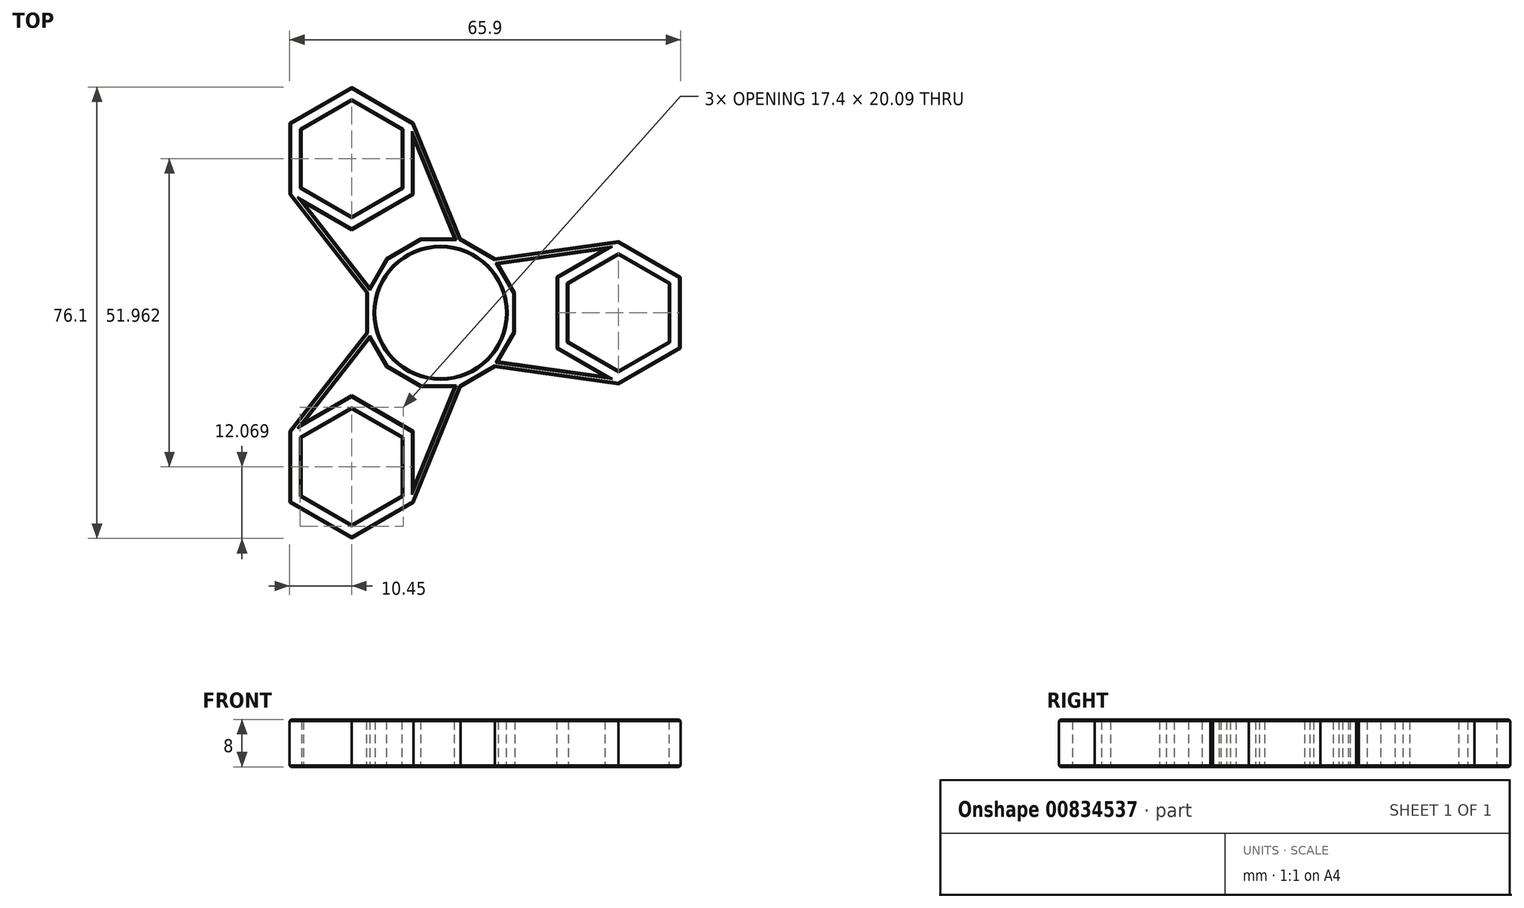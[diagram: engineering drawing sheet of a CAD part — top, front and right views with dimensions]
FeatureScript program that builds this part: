
annotation { "Feature Type Name" : "Feature", "Feature Type Description" : "" }
export const myFeature = defineFeature(function(context is Context, id is Id, definition is map)
    precondition{}
    {
        {
            var Q0;
            Q0=qCreatedBy(makeId("Top.planeOp"),FACE);
            var sketch = newSketch(context, id + "F0", { "sketchPlane" : qUnion([Q0])});
            skCircle(sketch, "E0", {"center": v(0, 0) * mm, "radius": 11.05 * mm});
            skCircle(sketch, "E1.cCircle", {"center": v(30, 0) * mm, "radius": 8.45 * mm, "construction": true});
            skLineSegment(sketch, "E1.0", {"start": v(30, 9.76) * mm, "end": v(38.45, 4.88) * mm});
            skLineSegment(sketch, "E1.1", {"start": v(38.45, 4.88) * mm, "end": v(38.45, -4.88) * mm});
            skLineSegment(sketch, "E1.2", {"start": v(38.45, -4.88) * mm, "end": v(30, -9.76) * mm});
            skLineSegment(sketch, "E1.3", {"start": v(30, -9.76) * mm, "end": v(21.55, -4.88) * mm});
            skLineSegment(sketch, "E1.4", {"start": v(21.55, -4.88) * mm, "end": v(21.55, 4.88) * mm});
            skLineSegment(sketch, "E1.5", {"start": v(21.55, 4.88) * mm, "end": v(30, 9.76) * mm});
            skPoint(sketch, "E1.0.midPoint", {"position": v(34.23, 7.32) * mm});
            skLineSegment(sketch, "E2.1.0", {"start": v(-15, 16.22) * mm, "end": v(-23.45, 21.1) * mm});
            skLineSegment(sketch, "E2.1.1", {"start": v(-6.55, 21.1) * mm, "end": v(-15, 16.22) * mm});
            skLineSegment(sketch, "E2.1.2", {"start": v(-23.45, 21.1) * mm, "end": v(-23.45, 30.86) * mm});
            skLineSegment(sketch, "E2.1.3", {"start": v(-23.45, 30.86) * mm, "end": v(-15, 35.74) * mm});
            skLineSegment(sketch, "E2.1.4", {"start": v(-15, 35.74) * mm, "end": v(-6.55, 30.86) * mm});
            skLineSegment(sketch, "E2.1.5", {"start": v(-6.55, 30.86) * mm, "end": v(-6.55, 21.1) * mm});
            skLineSegment(sketch, "E2.2.0", {"start": v(-6.55, -21.1) * mm, "end": v(-6.55, -30.86) * mm});
            skLineSegment(sketch, "E2.2.1", {"start": v(-15, -16.22) * mm, "end": v(-6.55, -21.1) * mm});
            skLineSegment(sketch, "E2.2.2", {"start": v(-6.55, -30.86) * mm, "end": v(-15, -35.74) * mm});
            skLineSegment(sketch, "E2.2.3", {"start": v(-15, -35.74) * mm, "end": v(-23.45, -30.86) * mm});
            skLineSegment(sketch, "E2.2.4", {"start": v(-23.45, -30.86) * mm, "end": v(-23.45, -21.1) * mm});
            skLineSegment(sketch, "E2.2.5", {"start": v(-23.45, -21.1) * mm, "end": v(-15, -16.22) * mm});
            skSolve(sketch);
        }
        {
            var Q0;
            Q0=qCreatedBy(makeId("Top.planeOp"),FACE);
            var sketch = newSketch(context, id + "F1", { "sketchPlane" : qUnion([Q0])});
            skLineSegment(sketch, "E3.0.0", {"start": v(-6.55, 21.1) * mm, "end": v(-6.55, 30.86) * mm});
            skLineSegment(sketch, "E3.0.1", {"start": v(-6.55, 30.86) * mm, "end": v(-15, 35.74) * mm});
            skLineSegment(sketch, "E3.0.2", {"start": v(-15, 35.74) * mm, "end": v(-23.45, 30.86) * mm});
            skLineSegment(sketch, "E3.0.3", {"start": v(-23.45, 30.86) * mm, "end": v(-23.45, 21.1) * mm});
            skLineSegment(sketch, "E3.0.4", {"start": v(-23.45, 21.1) * mm, "end": v(-15, 16.22) * mm});
            skLineSegment(sketch, "E3.0.5", {"start": v(-15, 16.22) * mm, "end": v(-6.55, 21.1) * mm});
            skLineSegment(sketch, "E4.0.0", {"start": v(-15, -16.22) * mm, "end": v(-23.45, -21.1) * mm});
            skLineSegment(sketch, "E4.0.1", {"start": v(-23.45, -21.1) * mm, "end": v(-23.45, -30.86) * mm});
            skLineSegment(sketch, "E4.0.2", {"start": v(-23.45, -30.86) * mm, "end": v(-15, -35.74) * mm});
            skLineSegment(sketch, "E4.0.3", {"start": v(-15, -35.74) * mm, "end": v(-6.55, -30.86) * mm});
            skLineSegment(sketch, "E4.0.4", {"start": v(-6.55, -30.86) * mm, "end": v(-6.55, -21.1) * mm});
            skLineSegment(sketch, "E4.0.5", {"start": v(-6.55, -21.1) * mm, "end": v(-15, -16.22) * mm});
            skLineSegment(sketch, "E5.0.0", {"start": v(30, 9.76) * mm, "end": v(21.55, 4.88) * mm});
            skLineSegment(sketch, "E5.0.1", {"start": v(21.55, 4.88) * mm, "end": v(21.55, -4.88) * mm});
            skLineSegment(sketch, "E5.0.2", {"start": v(21.55, -4.88) * mm, "end": v(30, -9.76) * mm});
            skLineSegment(sketch, "E5.0.3", {"start": v(30, -9.76) * mm, "end": v(38.45, -4.88) * mm});
            skLineSegment(sketch, "E5.0.4", {"start": v(38.45, -4.88) * mm, "end": v(38.45, 4.88) * mm});
            skLineSegment(sketch, "E5.0.5", {"start": v(38.45, 4.88) * mm, "end": v(30, 9.76) * mm});
            skCircle(sketch, "E6.0.0", {"center": v(0, 0) * mm, "radius": 11.05 * mm});
            skLineSegment(sketch, "E7", {"start": v(-23.45, 30.86) * mm, "end": v(-6.55, 21.1) * mm, "construction": true});
            skLineSegment(sketch, "E8", {"start": v(-23.45, -30.86) * mm, "end": v(-6.55, -21.1) * mm, "construction": true});
            skLineSegment(sketch, "E9", {"start": v(21.55, 4.88) * mm, "end": v(38.45, -4.88) * mm, "construction": true});
            skLineSegment(sketch, "E10.0", {"start": v(40.45, -6.03) * mm, "end": v(40.45, 6.03) * mm});
            skLineSegment(sketch, "E10.1", {"start": v(30, 12.07) * mm, "end": v(19.55, 6.03) * mm});
            skLineSegment(sketch, "E10.2", {"start": v(19.55, 6.03) * mm, "end": v(19.55, -6.03) * mm});
            skLineSegment(sketch, "E10.3", {"start": v(40.45, 6.03) * mm, "end": v(30, 12.07) * mm});
            skLineSegment(sketch, "E10.4", {"start": v(19.55, -6.03) * mm, "end": v(30, -12.07) * mm});
            skLineSegment(sketch, "E10.5", {"start": v(30, -12.07) * mm, "end": v(40.45, -6.03) * mm});
            skCircle(sketch, "E11.cCircle", {"center": v(0, 0) * mm, "radius": 12.5 * mm, "construction": true});
            skLineSegment(sketch, "E11.0", {"start": v(3.35, 12.5) * mm, "end": v(9.15, 9.15) * mm});
            skLineSegment(sketch, "E11.1", {"start": v(9.15, 9.15) * mm, "end": v(12.5, 3.35) * mm});
            skLineSegment(sketch, "E11.2", {"start": v(12.5, 3.35) * mm, "end": v(12.5, -3.35) * mm});
            skLineSegment(sketch, "E11.3", {"start": v(12.5, -3.35) * mm, "end": v(9.15, -9.15) * mm});
            skLineSegment(sketch, "E11.4", {"start": v(9.15, -9.15) * mm, "end": v(3.35, -12.5) * mm});
            skLineSegment(sketch, "E11.5", {"start": v(3.35, -12.5) * mm, "end": v(-3.35, -12.5) * mm});
            skLineSegment(sketch, "E11.6", {"start": v(-3.35, -12.5) * mm, "end": v(-9.15, -9.15) * mm});
            skLineSegment(sketch, "E11.7", {"start": v(-9.15, -9.15) * mm, "end": v(-12.5, -3.35) * mm});
            skLineSegment(sketch, "E11.8", {"start": v(-12.5, -3.35) * mm, "end": v(-12.5, 3.35) * mm});
            skLineSegment(sketch, "E11.9", {"start": v(-12.5, 3.35) * mm, "end": v(-9.15, 9.15) * mm});
            skLineSegment(sketch, "E11.10", {"start": v(-9.15, 9.15) * mm, "end": v(-3.35, 12.5) * mm});
            skLineSegment(sketch, "E11.11", {"start": v(-3.35, 12.5) * mm, "end": v(3.35, 12.5) * mm});
            skPoint(sketch, "E11.0.midPoint", {"position": v(6.25, 10.83) * mm});
            skLineSegment(sketch, "E12", {"start": v(30, 12.07) * mm, "end": v(9.15, 9.15) * mm});
            skLineSegment(sketch, "E13", {"start": v(30, -12.07) * mm, "end": v(9.15, -9.15) * mm});
            skLineSegment(sketch, "E14.0", {"start": v(30.14, 11.08) * mm, "end": v(9.29, 8.16) * mm});
            skLineSegment(sketch, "E15.0", {"start": v(30.14, -11.08) * mm, "end": v(9.29, -8.16) * mm});
            skLineSegment(sketch, "E16.0", {"start": v(-25.45, -19.95) * mm, "end": v(-25.45, -32.01) * mm});
            skLineSegment(sketch, "E16.1", {"start": v(-15, -38.05) * mm, "end": v(-4.55, -32.01) * mm});
            skLineSegment(sketch, "E16.2", {"start": v(-4.55, -32.01) * mm, "end": v(-4.55, -19.95) * mm});
            skLineSegment(sketch, "E16.3", {"start": v(-25.45, -32.01) * mm, "end": v(-15, -38.05) * mm});
            skLineSegment(sketch, "E16.4", {"start": v(-4.55, -19.95) * mm, "end": v(-15, -13.91) * mm});
            skLineSegment(sketch, "E16.5", {"start": v(-15, -13.91) * mm, "end": v(-25.45, -19.95) * mm});
            skLineSegment(sketch, "E17.0", {"start": v(-4.55, 19.95) * mm, "end": v(-4.55, 32.01) * mm});
            skLineSegment(sketch, "E17.1", {"start": v(-15, 38.05) * mm, "end": v(-25.45, 32.01) * mm});
            skLineSegment(sketch, "E17.2", {"start": v(-25.45, 32.01) * mm, "end": v(-25.45, 19.95) * mm});
            skLineSegment(sketch, "E17.3", {"start": v(-4.55, 32.01) * mm, "end": v(-15, 38.05) * mm});
            skLineSegment(sketch, "E17.4", {"start": v(-25.45, 19.95) * mm, "end": v(-15, 13.91) * mm});
            skLineSegment(sketch, "E17.5", {"start": v(-15, 13.91) * mm, "end": v(-4.55, 19.95) * mm});
            skLineSegment(sketch, "E18", {"start": v(-25.45, 19.95) * mm, "end": v(-12.5, 3.35) * mm});
            skLineSegment(sketch, "E19", {"start": v(-4.55, 32.01) * mm, "end": v(3.35, 12.5) * mm});
            skLineSegment(sketch, "E20", {"start": v(-25.45, -19.95) * mm, "end": v(-12.5, -3.35) * mm});
            skLineSegment(sketch, "E21", {"start": v(3.35, -12.5) * mm, "end": v(-4.55, -32.01) * mm});
            skLineSegment(sketch, "E22.0", {"start": v(-24.66, 20.56) * mm, "end": v(-11.71, 3.96) * mm});
            skLineSegment(sketch, "E23.0", {"start": v(-5.48, 31.64) * mm, "end": v(2.42, 12.12) * mm});
            skLineSegment(sketch, "E24.0", {"start": v(-24.66, -20.56) * mm, "end": v(-11.71, -3.96) * mm});
            skLineSegment(sketch, "E25.0", {"start": v(2.42, -12.12) * mm, "end": v(-5.48, -31.64) * mm});
            skSolve(sketch);
        }
        {
            var Q0;
            Q0=makeQuery(id+"F1.imprint","IMPRINT",FACE,{"disambiguationData":[TD([[makeQuery(id+"F1.imprint","IMPRINT",EDGE,{"derivedFrom":sQuery(id+"F1.wireOp",EDGE,"E6.0.0")}),-1.0]])]});
            var Q1;
            Q1=makeQuery(id+"F1.imprint","IMPRINT",FACE,{"disambiguationData":[TD([[makeQuery(id+"F1.imprint","IMPRINT",EDGE,{"derivedFrom":sQuery(id+"F1.wireOp",EDGE,"E5.0.0")}),-1.0]])]});
            var Q2;
            {var subQ0=sQuery(id+"F1.wireOp",EDGE,"E13");Q2=makeQuery(id+"F1.imprint","IMPRINT",FACE,{"disambiguationData":[TD([[makeQuery(id+"F1.imprint","IMPRINT",EDGE,{"derivedFrom":subQ0}),-1.0]])]});}
            var Q3;
            {var subQ0=sQuery(id+"F1.wireOp",EDGE,"E12");Q3=makeQuery(id+"F1.imprint","IMPRINT",FACE,{"disambiguationData":[TD([[makeQuery(id+"F1.imprint","IMPRINT",EDGE,{"derivedFrom":subQ0}),1.0]])]});}
            var Q4;
            Q4=makeQuery(id+"F1.imprint","IMPRINT",FACE,{"disambiguationData":[TD([[makeQuery(id+"F1.imprint","IMPRINT",EDGE,{"derivedFrom":sQuery(id+"F1.wireOp",EDGE,"E4.0.0")}),-1.0]])]});
            var Q5;
            Q5=makeQuery(id+"F1.imprint","IMPRINT",FACE,{"disambiguationData":[TD([[makeQuery(id+"F1.imprint","IMPRINT",EDGE,{"derivedFrom":sQuery(id+"F1.wireOp",EDGE,"E3.0.0")}),-1.0]])]});
            var Q6;
            Q6=makeQuery(id+"F1.imprint","IMPRINT",FACE,{"disambiguationData":[TD([[makeQuery(id+"F1.imprint","IMPRINT",EDGE,{"derivedFrom":sQuery(id+"F1.wireOp",EDGE,"E11.9")}),1.0]])]});
            var Q7;
            Q7=makeQuery(id+"F1.imprint","IMPRINT",FACE,{"disambiguationData":[TD([[makeQuery(id+"F1.imprint","IMPRINT",EDGE,{"derivedFrom":sQuery(id+"F1.wireOp",EDGE,"E11.11")}),1.0]])]});
            var Q8;
            {var subQ0=sQuery(id+"F1.wireOp",EDGE,"E20");Q8=makeQuery(id+"F1.imprint","IMPRINT",FACE,{"disambiguationData":[TD([[makeQuery(id+"F1.imprint","IMPRINT",EDGE,{"derivedFrom":subQ0}),-1.0]])]});}
            var Q9;
            {var subQ0=sQuery(id+"F1.wireOp",EDGE,"E21");Q9=makeQuery(id+"F1.imprint","IMPRINT",FACE,{"disambiguationData":[TD([[makeQuery(id+"F1.imprint","IMPRINT",EDGE,{"derivedFrom":subQ0}),-1.0]])]});}
            extrude(context, id + "F2", {"entities" : qUnion([Q0, Q1, Q2, Q3, Q4, Q5, Q6, Q7, Q8, Q9]), "depth" : 8 * mm, "offsetDistance" : 25 * mm});
        }
        {
            var Q0;
            Q0=makeQuery(id+"F2.opExtrude","CAP_FACE",FACE,{"disambiguationData":[OSD([sQuery(id+"F1.wireOp",EDGE,"E3.0.0"),sQuery(id+"F1.wireOp",EDGE,"E3.0.1"),sQuery(id+"F1.wireOp",EDGE,"E3.0.2"),sQuery(id+"F1.wireOp",EDGE,"E3.0.3"),sQuery(id+"F1.wireOp",EDGE,"E3.0.4"),sQuery(id+"F1.wireOp",EDGE,"E3.0.5"),sQuery(id+"F1.wireOp",EDGE,"E4.0.0"),sQuery(id+"F1.wireOp",EDGE,"E4.0.1"),sQuery(id+"F1.wireOp",EDGE,"E4.0.2"),sQuery(id+"F1.wireOp",EDGE,"E4.0.3"),sQuery(id+"F1.wireOp",EDGE,"E4.0.4"),sQuery(id+"F1.wireOp",EDGE,"E4.0.5"),sQuery(id+"F1.wireOp",EDGE,"E5.0.0"),sQuery(id+"F1.wireOp",EDGE,"E5.0.1"),sQuery(id+"F1.wireOp",EDGE,"E5.0.2"),sQuery(id+"F1.wireOp",EDGE,"E5.0.3"),sQuery(id+"F1.wireOp",EDGE,"E5.0.4"),sQuery(id+"F1.wireOp",EDGE,"E5.0.5"),sQuery(id+"F1.wireOp",EDGE,"E6.0.0"),sQuery(id+"F1.wireOp",EDGE,"E10.0"),sQuery(id+"F1.wireOp",EDGE,"E10.1"),sQuery(id+"F1.wireOp",EDGE,"E10.2"),sQuery(id+"F1.wireOp",EDGE,"E10.3"),sQuery(id+"F1.wireOp",EDGE,"E10.4"),sQuery(id+"F1.wireOp",EDGE,"E10.5"),sQuery(id+"F1.wireOp",EDGE,"E11.0"),sQuery(id+"F1.wireOp",EDGE,"E11.1"),sQuery(id+"F1.wireOp",EDGE,"E11.2"),sQuery(id+"F1.wireOp",EDGE,"E11.3"),sQuery(id+"F1.wireOp",EDGE,"E11.4"),sQuery(id+"F1.wireOp",EDGE,"E11.5"),sQuery(id+"F1.wireOp",EDGE,"E11.6"),sQuery(id+"F1.wireOp",EDGE,"E11.7"),sQuery(id+"F1.wireOp",EDGE,"E11.8"),sQuery(id+"F1.wireOp",EDGE,"E11.9"),sQuery(id+"F1.wireOp",EDGE,"E11.10"),sQuery(id+"F1.wireOp",EDGE,"E11.11"),sQuery(id+"F1.wireOp",EDGE,"E12"),sQuery(id+"F1.wireOp",EDGE,"E13"),sQuery(id+"F1.wireOp",EDGE,"E14.0"),sQuery(id+"F1.wireOp",EDGE,"E15.0"),sQuery(id+"F1.wireOp",EDGE,"E16.0"),sQuery(id+"F1.wireOp",EDGE,"E16.1"),sQuery(id+"F1.wireOp",EDGE,"E16.2"),sQuery(id+"F1.wireOp",EDGE,"E16.3"),sQuery(id+"F1.wireOp",EDGE,"E16.4"),sQuery(id+"F1.wireOp",EDGE,"E16.5"),sQuery(id+"F1.wireOp",EDGE,"E17.0"),sQuery(id+"F1.wireOp",EDGE,"E17.1"),sQuery(id+"F1.wireOp",EDGE,"E17.2"),sQuery(id+"F1.wireOp",EDGE,"E17.3"),sQuery(id+"F1.wireOp",EDGE,"E17.4"),sQuery(id+"F1.wireOp",EDGE,"E17.5"),sQuery(id+"F1.wireOp",EDGE,"E18"),sQuery(id+"F1.wireOp",EDGE,"E19"),sQuery(id+"F1.wireOp",EDGE,"E20"),sQuery(id+"F1.wireOp",EDGE,"E21"),sQuery(id+"F1.wireOp",EDGE,"E22.0"),sQuery(id+"F1.wireOp",EDGE,"E23.0"),sQuery(id+"F1.wireOp",EDGE,"E24.0"),sQuery(id+"F1.wireOp",EDGE,"E25.0")])],"isStart":true});
            var Q1;
            Q1=makeQuery(id+"F2.opExtrude","CAP_FACE",FACE,{"disambiguationData":[OSD([sQuery(id+"F1.wireOp",EDGE,"E3.0.0"),sQuery(id+"F1.wireOp",EDGE,"E3.0.1"),sQuery(id+"F1.wireOp",EDGE,"E3.0.2"),sQuery(id+"F1.wireOp",EDGE,"E3.0.3"),sQuery(id+"F1.wireOp",EDGE,"E3.0.4"),sQuery(id+"F1.wireOp",EDGE,"E3.0.5"),sQuery(id+"F1.wireOp",EDGE,"E4.0.0"),sQuery(id+"F1.wireOp",EDGE,"E4.0.1"),sQuery(id+"F1.wireOp",EDGE,"E4.0.2"),sQuery(id+"F1.wireOp",EDGE,"E4.0.3"),sQuery(id+"F1.wireOp",EDGE,"E4.0.4"),sQuery(id+"F1.wireOp",EDGE,"E4.0.5"),sQuery(id+"F1.wireOp",EDGE,"E5.0.0"),sQuery(id+"F1.wireOp",EDGE,"E5.0.1"),sQuery(id+"F1.wireOp",EDGE,"E5.0.2"),sQuery(id+"F1.wireOp",EDGE,"E5.0.3"),sQuery(id+"F1.wireOp",EDGE,"E5.0.4"),sQuery(id+"F1.wireOp",EDGE,"E5.0.5"),sQuery(id+"F1.wireOp",EDGE,"E6.0.0"),sQuery(id+"F1.wireOp",EDGE,"E10.0"),sQuery(id+"F1.wireOp",EDGE,"E10.1"),sQuery(id+"F1.wireOp",EDGE,"E10.2"),sQuery(id+"F1.wireOp",EDGE,"E10.3"),sQuery(id+"F1.wireOp",EDGE,"E10.4"),sQuery(id+"F1.wireOp",EDGE,"E10.5"),sQuery(id+"F1.wireOp",EDGE,"E11.0"),sQuery(id+"F1.wireOp",EDGE,"E11.1"),sQuery(id+"F1.wireOp",EDGE,"E11.2"),sQuery(id+"F1.wireOp",EDGE,"E11.3"),sQuery(id+"F1.wireOp",EDGE,"E11.4"),sQuery(id+"F1.wireOp",EDGE,"E11.5"),sQuery(id+"F1.wireOp",EDGE,"E11.6"),sQuery(id+"F1.wireOp",EDGE,"E11.7"),sQuery(id+"F1.wireOp",EDGE,"E11.8"),sQuery(id+"F1.wireOp",EDGE,"E11.9"),sQuery(id+"F1.wireOp",EDGE,"E11.10"),sQuery(id+"F1.wireOp",EDGE,"E11.11"),sQuery(id+"F1.wireOp",EDGE,"E12"),sQuery(id+"F1.wireOp",EDGE,"E13"),sQuery(id+"F1.wireOp",EDGE,"E14.0"),sQuery(id+"F1.wireOp",EDGE,"E15.0"),sQuery(id+"F1.wireOp",EDGE,"E16.0"),sQuery(id+"F1.wireOp",EDGE,"E16.1"),sQuery(id+"F1.wireOp",EDGE,"E16.2"),sQuery(id+"F1.wireOp",EDGE,"E16.3"),sQuery(id+"F1.wireOp",EDGE,"E16.4"),sQuery(id+"F1.wireOp",EDGE,"E16.5"),sQuery(id+"F1.wireOp",EDGE,"E17.0"),sQuery(id+"F1.wireOp",EDGE,"E17.1"),sQuery(id+"F1.wireOp",EDGE,"E17.2"),sQuery(id+"F1.wireOp",EDGE,"E17.3"),sQuery(id+"F1.wireOp",EDGE,"E17.4"),sQuery(id+"F1.wireOp",EDGE,"E17.5"),sQuery(id+"F1.wireOp",EDGE,"E18"),sQuery(id+"F1.wireOp",EDGE,"E19"),sQuery(id+"F1.wireOp",EDGE,"E20"),sQuery(id+"F1.wireOp",EDGE,"E21"),sQuery(id+"F1.wireOp",EDGE,"E22.0"),sQuery(id+"F1.wireOp",EDGE,"E23.0"),sQuery(id+"F1.wireOp",EDGE,"E24.0"),sQuery(id+"F1.wireOp",EDGE,"E25.0")])],"isStart":false});
            chamfer(context, id + "F3", {"entities" : qUnion([Q0, Q1]), "width" : 0.25 * mm, "tangentPropagation" : true});
        }
    });
